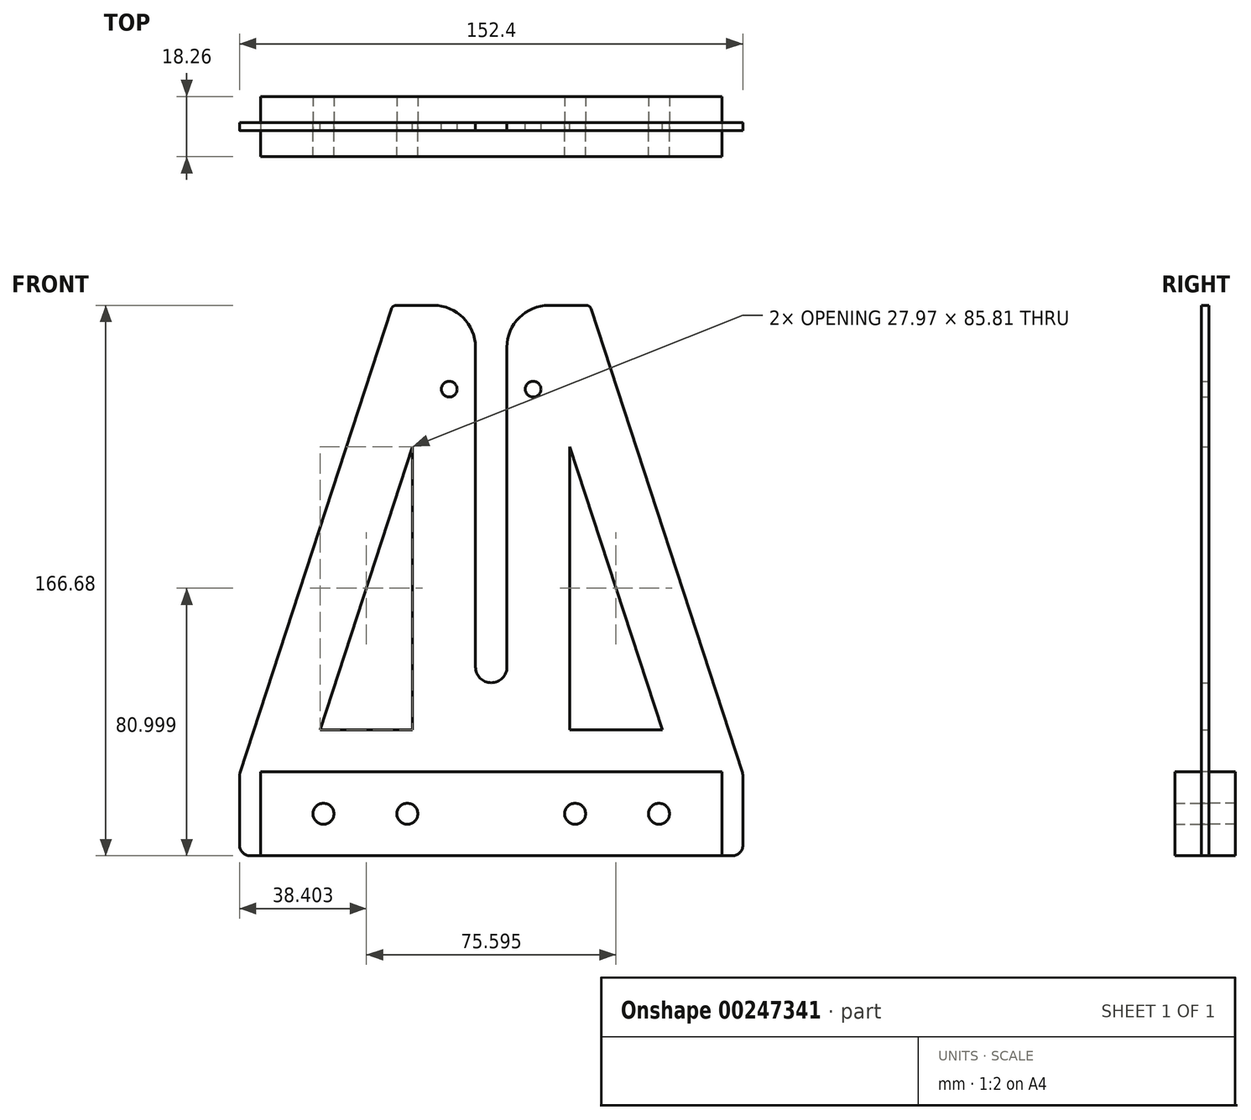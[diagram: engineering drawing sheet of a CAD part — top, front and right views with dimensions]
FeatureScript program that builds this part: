
annotation { "Feature Type Name" : "Feature", "Feature Type Description" : "" }
export const myFeature = defineFeature(function(context is Context, id is Id, definition is map)
    precondition{}
    {
        {
            var Q0;
            Q0=qCreatedBy(makeId("Front.planeOp"),FACE);
            var sketch = newSketch(context, id + "F0", { "sketchPlane" : qUnion([Q0])});
            skLineSegment(sketch, "E0.bottom", {"start": v(-76.2, -83.34) * mm, "end": v(73.03, -83.34) * mm});
            skLineSegment(sketch, "E0.top", {"start": v(17.46, 83.34) * mm, "end": v(28.75, 83.34) * mm});
            skLineSegment(sketch, "E0.left", {"start": v(-76.2, -83.34) * mm, "end": v(-76.2, -59.19) * mm});
            skLineSegment(sketch, "E0.right", {"start": v(76.2, -80.17) * mm, "end": v(76.2, -59.19) * mm});
            skPoint(sketch, "E0.middle", {"position": v(0, 0) * mm});
            skLineSegment(sketch, "E1", {"start": v(0, 83.34) * mm, "end": v(0, -83.34) * mm, "construction": true});
            skLineSegment(sketch, "E2", {"start": v(-76.2, -70.64) * mm, "end": v(76.2, -70.64) * mm, "construction": true});
            skCircle(sketch, "E3", {"center": v(-50.8, -70.64) * mm, "radius": 3.18 * mm});
            skCircle(sketch, "E4", {"center": v(-25.4, -70.64) * mm, "radius": 3.18 * mm});
            skCircle(sketch, "E5", {"center": v(25.4, -70.64) * mm, "radius": 3.18 * mm});
            skCircle(sketch, "E6", {"center": v(50.8, -70.64) * mm, "radius": 3.18 * mm});
            skArc(sketch, "E7", {"start": v(-4.76, -26.2) * mm, "mid": v(0, -30.96) * mm, "end": v(4.76, -26.2) * mm});
            skLineSegment(sketch, "E8", {"start": v(30.26, 82.25) * mm, "end": v(76.04, -58.2) * mm});
            skLineSegment(sketch, "E9", {"start": v(-4.76, 70.64) * mm, "end": v(-4.76, -26.2) * mm});
            skLineSegment(sketch, "E10", {"start": v(4.76, 70.64) * mm, "end": v(4.76, -26.2) * mm});
            skPoint(sketch, "E11.newPointA", {"position": v(4.76, 82.55) * mm});
            skPoint(sketch, "E11.newPointB", {"position": v(-76.2, 83.34) * mm});
            skArc(sketch, "E11.filletArc", {"start": v(17.46, 83.34) * mm, "mid": v(8.48, 79.62) * mm, "end": v(4.76, 70.64) * mm});
            skPoint(sketch, "E12.newPointA", {"position": v(76.2, 83.34) * mm});
            skPoint(sketch, "E12.newPointB", {"position": v(30.16, 82.55) * mm});
            skArc(sketch, "E12.filletArc", {"start": v(30.26, 82.25) * mm, "mid": v(29.68, 83.04) * mm, "end": v(28.75, 83.34) * mm});
            skPoint(sketch, "E13.newPointA", {"position": v(75.96, -57.94) * mm});
            skArc(sketch, "E13.filletArc", {"start": v(76.2, -59.19) * mm, "mid": v(76.16, -58.7) * mm, "end": v(76.04, -58.2) * mm});
            skPoint(sketch, "E14.visualSharp", {"position": v(76.2, -83.34) * mm});
            skArc(sketch, "E14.filletArc", {"start": v(73.03, -83.34) * mm, "mid": v(75.27, -82.41) * mm, "end": v(76.2, -80.17) * mm});
            skArc(sketch, "E15.MirrorCS", {"start": v(-73.03, -83.34) * mm, "mid": v(-75.27, -82.41) * mm, "end": v(-76.2, -80.17) * mm});
            skArc(sketch, "E16.MirrorCS", {"start": v(-30.26, 82.25) * mm, "mid": v(-29.68, 83.04) * mm, "end": v(-28.75, 83.34) * mm});
            skArc(sketch, "E17.MirrorCS", {"start": v(-76.2, -59.19) * mm, "mid": v(-76.16, -58.7) * mm, "end": v(-76.04, -58.2) * mm});
            skLineSegment(sketch, "E18.MirrorCS", {"start": v(-76.2, -80.17) * mm, "end": v(-76.2, -59.19) * mm});
            skLineSegment(sketch, "E19.MirrorCS", {"start": v(-17.46, 83.34) * mm, "end": v(-28.75, 83.34) * mm});
            skArc(sketch, "E20.MirrorCS", {"start": v(-17.46, 83.34) * mm, "mid": v(-8.48, 79.62) * mm, "end": v(-4.76, 70.64) * mm});
            skPoint(sketch, "E21.MirrorP", {"position": v(-75.96, -57.94) * mm});
            skLineSegment(sketch, "E22.MirrorCS", {"start": v(-30.26, 82.25) * mm, "end": v(-76.04, -58.2) * mm});
            skPoint(sketch, "E23.MirrorP", {"position": v(-4.76, 82.55) * mm});
            skPoint(sketch, "E24.MirrorP", {"position": v(-30.16, 82.55) * mm});
            skPoint(sketch, "E25.MirrorP", {"position": v(-76.2, -83.34) * mm});
            skPoint(sketch, "E26.orphan", {"position": v(4.76, -70.64) * mm});
            skPoint(sketch, "E27.orphan", {"position": v(-4.76, -70.64) * mm});
            skLineSegment(sketch, "E28", {"start": v(12.7, 71.21) * mm, "end": v(12.7, -70.64) * mm, "construction": true});
            skCircle(sketch, "E29", {"center": v(12.7, 57.94) * mm, "radius": 2.38 * mm});
            skCircle(sketch, "E30.MirrorC", {"center": v(-12.7, 57.94) * mm, "radius": 2.38 * mm});
            skLineSegment(sketch, "E31", {"start": v(-23.81, 40.56) * mm, "end": v(-51.78, -45.24) * mm});
            skLineSegment(sketch, "E32", {"start": v(-51.78, -45.24) * mm, "end": v(-23.81, -45.24) * mm});
            skLineSegment(sketch, "E33", {"start": v(-23.81, -45.24) * mm, "end": v(-23.81, 40.56) * mm});
            skLineSegment(sketch, "E34.MirrorCS", {"start": v(23.81, -45.24) * mm, "end": v(23.81, 40.56) * mm});
            skLineSegment(sketch, "E35.MirrorCS", {"start": v(51.78, -45.24) * mm, "end": v(23.81, -45.24) * mm});
            skLineSegment(sketch, "E36.MirrorCS", {"start": v(23.81, 40.56) * mm, "end": v(51.78, -45.24) * mm});
            skSolve(sketch);
        }
        {
            var Q0;
            Q0=makeQuery(id+"F0.imprint","IMPRINT",FACE,{"disambiguationData":[TD([[makeQuery(id+"F0.imprint","IMPRINT",EDGE,{"derivedFrom":sQuery(id+"F0.wireOp",EDGE,"E0.top")}),-1.0]])]});
            extrude(context, id + "F1", {"entities" : qUnion([Q0]), "depth" : 2.38 * mm});
        }
        {
            var Q0;
            Q0=makeQuery(id+"F1.opExtrude","CAP_FACE",FACE,{"disambiguationData":[OSD([sQuery(id+"F0.wireOp",EDGE,"E0.bottom"),sQuery(id+"F0.wireOp",EDGE,"E0.top"),sQuery(id+"F0.wireOp",EDGE,"E0.left"),sQuery(id+"F0.wireOp",EDGE,"E0.right"),sQuery(id+"F0.wireOp",EDGE,"E5"),sQuery(id+"F0.wireOp",EDGE,"E6"),sQuery(id+"F0.wireOp",EDGE,"E7"),sQuery(id+"F0.wireOp",EDGE,"E10"),sQuery(id+"F0.wireOp",EDGE,"E11.filletArc"),sQuery(id+"F0.wireOp",EDGE,"E12.filletArc"),sQuery(id+"F0.wireOp",EDGE,"E13.filletArc"),sQuery(id+"F0.wireOp",EDGE,"E14.filletArc"),sQuery(id+"F0.wireOp",EDGE,"E16.MirrorCS"),sQuery(id+"F0.wireOp",EDGE,"E17.MirrorCS"),sQuery(id+"F0.wireOp",EDGE,"E18.MirrorCS"),sQuery(id+"F0.wireOp",EDGE,"E19.MirrorCS"),sQuery(id+"F0.wireOp",EDGE,"E3"),sQuery(id+"F0.wireOp",EDGE,"E20.MirrorCS"),sQuery(id+"F0.wireOp",EDGE,"E22.MirrorCS"),sQuery(id+"F0.wireOp",EDGE,"E9"),sQuery(id+"F0.wireOp",EDGE,"E4"),sQuery(id+"F0.wireOp",EDGE,"E29"),sQuery(id+"F0.wireOp",EDGE,"E30.MirrorC"),sQuery(id+"F0.wireOp",EDGE,"E31"),sQuery(id+"F0.wireOp",EDGE,"E32"),sQuery(id+"F0.wireOp",EDGE,"E33"),sQuery(id+"F0.wireOp",EDGE,"E8"),sQuery(id+"F0.wireOp",EDGE,"E34.MirrorCS"),sQuery(id+"F0.wireOp",EDGE,"E35.MirrorCS"),sQuery(id+"F0.wireOp",EDGE,"E36.MirrorCS")])],"isStart":false});
            var sketch = newSketch(context, id + "F2", { "sketchPlane" : qUnion([Q0])});
            skLineSegment(sketch, "E37", {"start": v(-25.4, -70.64) * mm, "end": v(25.4, -70.64) * mm, "construction": true});
            skLineSegment(sketch, "E38.bottom", {"start": v(-69.85, -83.34) * mm, "end": v(69.85, -83.34) * mm});
            skLineSegment(sketch, "E38.top", {"start": v(-69.85, -57.94) * mm, "end": v(69.85, -57.94) * mm});
            skLineSegment(sketch, "E38.left", {"start": v(-69.85, -83.34) * mm, "end": v(-69.85, -57.94) * mm});
            skLineSegment(sketch, "E38.right", {"start": v(69.85, -83.34) * mm, "end": v(69.85, -57.94) * mm});
            skPoint(sketch, "E38.middle", {"position": v(0, -70.64) * mm});
            skCircle(sketch, "E39", {"center": v(-50.8, -70.64) * mm, "radius": 3.18 * mm});
            skCircle(sketch, "E40", {"center": v(-25.4, -70.64) * mm, "radius": 3.18 * mm});
            skCircle(sketch, "E41", {"center": v(25.4, -70.64) * mm, "radius": 3.18 * mm});
            skCircle(sketch, "E42", {"center": v(50.8, -70.64) * mm, "radius": 3.18 * mm});
            skSolve(sketch);
        }
        {
            var Q0;
            Q0 = qSketchRegion(id + "F2", true);
            extrude(context, id + "F3", {"entities" : qUnion([Q0]), "depth" : 7.94 * mm});
        }
        {
            var Q0;
            Q0=makeQuery(id+"F2.imprint","IMPRINT",FACE,{"disambiguationData":[TD([[makeQuery(id+"F2.imprint","IMPRINT",EDGE,{"derivedFrom":sQuery(id+"F2.wireOp",EDGE,"E38.bottom")}),1.0]])]});
            extrude(context, id + "F4", {"entities" : qUnion([Q0]), "oppositeDirection" : true, "depth" : 10.32 * mm});
        }
    });
